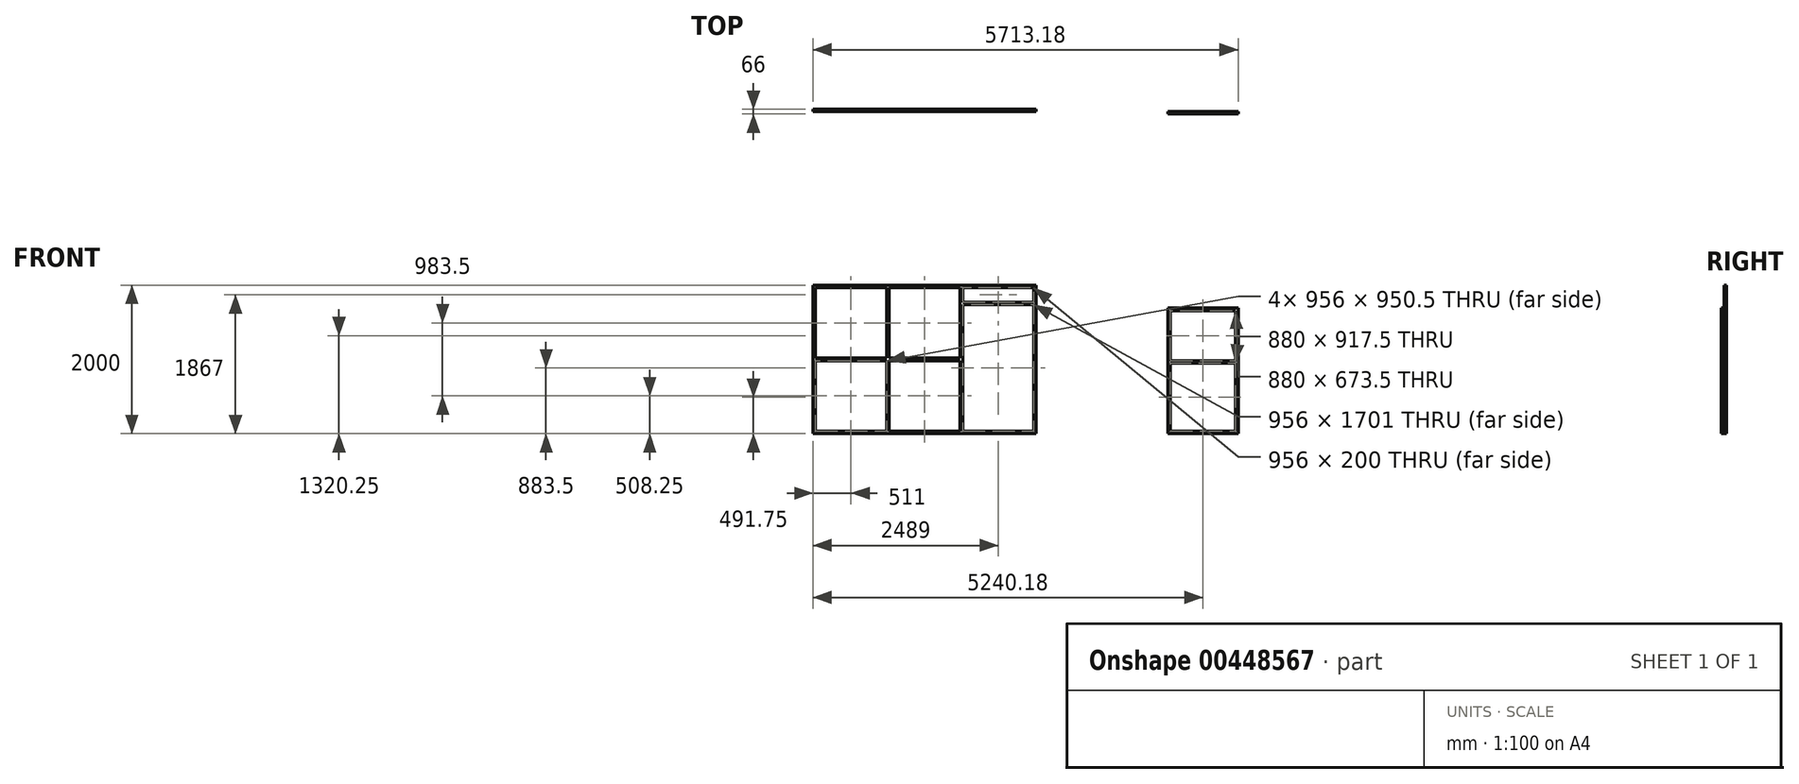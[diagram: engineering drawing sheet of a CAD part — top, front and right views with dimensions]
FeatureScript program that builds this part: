
annotation { "Feature Type Name" : "Feature", "Feature Type Description" : "" }
export const myFeature = defineFeature(function(context is Context, id is Id, definition is map)
    precondition{}
    {
        {
            var Q0;
            Q0=qCreatedBy(makeId("Front.planeOp"),FACE);
            var sketch = newSketch(context, id + "F0", { "sketchPlane" : qUnion([Q0])});
            skLineSegment(sketch, "E0.bottom", {"start": v(0, 0) * mm, "end": v(3000, 0) * mm});
            skLineSegment(sketch, "E0.top", {"start": v(0, 2000) * mm, "end": v(3000, 2000) * mm});
            skLineSegment(sketch, "E0.left", {"start": v(0, 0) * mm, "end": v(0, 2000) * mm});
            skLineSegment(sketch, "E0.right", {"start": v(3000, 0) * mm, "end": v(3000, 2000) * mm});
            skLineSegment(sketch, "E1.0", {"start": v(33, 33) * mm, "end": v(33, 1967) * mm});
            skLineSegment(sketch, "E1.1", {"start": v(33, 33) * mm, "end": v(2967, 33) * mm});
            skLineSegment(sketch, "E1.2", {"start": v(2967, 33) * mm, "end": v(2967, 1734) * mm});
            skLineSegment(sketch, "E1.3", {"start": v(33, 1967) * mm, "end": v(1978, 1967) * mm});
            skLineSegment(sketch, "E2.bottom", {"start": v(989, 1967) * mm, "end": v(1022, 1967) * mm});
            skLineSegment(sketch, "E2.top", {"start": v(989, 33) * mm, "end": v(1022, 33) * mm});
            skLineSegment(sketch, "E2.left", {"start": v(989, 1967) * mm, "end": v(989, 1016.5) * mm});
            skLineSegment(sketch, "E2.right", {"start": v(1022, 1967) * mm, "end": v(1022, 1016.5) * mm});
            skLineSegment(sketch, "E3.left", {"start": v(1978, 1967) * mm, "end": v(1978, 1016.5) * mm});
            skLineSegment(sketch, "E3.right", {"start": v(2011, 1967) * mm, "end": v(2011, 1767) * mm});
            skLineSegment(sketch, "E4.bottom", {"start": v(33, 1016.5) * mm, "end": v(989, 1016.5) * mm});
            skLineSegment(sketch, "E4.top", {"start": v(33, 983.5) * mm, "end": v(989, 983.5) * mm});
            skLineSegment(sketch, "E4.left", {"start": v(33, 1016.5) * mm, "end": v(33, 983.5) * mm});
            skLineSegment(sketch, "E4.right", {"start": v(2967, 1016.5) * mm, "end": v(2967, 983.5) * mm});
            skLineSegment(sketch, "E5.trimOffspring", {"start": v(1022, 983.5) * mm, "end": v(1978, 983.5) * mm});
            skLineSegment(sketch, "E6.trimOffspring", {"start": v(1022, 1016.5) * mm, "end": v(1978, 1016.5) * mm});
            skLineSegment(sketch, "E7.bottom", {"start": v(2011, 1767) * mm, "end": v(2967, 1767) * mm});
            skLineSegment(sketch, "E7.top", {"start": v(2011, 1734) * mm, "end": v(2967, 1734) * mm});
            skLineSegment(sketch, "E8.trimOffspring", {"start": v(1978, 983.5) * mm, "end": v(1978, 33) * mm});
            skLineSegment(sketch, "E9.trimOffspring", {"start": v(1022, 983.5) * mm, "end": v(1022, 33) * mm});
            skLineSegment(sketch, "E10.trimOffspring", {"start": v(989, 983.5) * mm, "end": v(989, 33) * mm});
            skLineSegment(sketch, "E11.trimOffspring", {"start": v(2011, 1734) * mm, "end": v(2011, 33) * mm});
            skLineSegment(sketch, "E12.trimOffspring", {"start": v(2967, 1767) * mm, "end": v(2967, 1967) * mm});
            skLineSegment(sketch, "E13.trimOffspring", {"start": v(2011, 1967) * mm, "end": v(2967, 1967) * mm});
            skSolve(sketch);
        }
        {
            var Q0;
            Q0 = qSketchRegion(id + "F0", true);
            var Q1;
            {var subQ5=sQuery(id+"F0.wireOp",EDGE,"E4.left");Q1=makeQuery(id+"F0.imprint","IMPRINT",FACE,{"disambiguationData":[TD([[makeQuery(id+"F0.imprint","IMPRINT",EDGE,{"derivedFrom":subQ5}),1.0]])]});}
            var Q2;
            {var subQ5=sQuery(id+"F0.wireOp",EDGE,"E2.bottom");Q2=makeQuery(id+"F0.imprint","IMPRINT",FACE,{"disambiguationData":[TD([[makeQuery(id+"F0.imprint","IMPRINT",EDGE,{"derivedFrom":subQ5}),-1.0]])]});}
            var Q3;
            Q3=makeQuery(id+"F0.imprint","IMPRINT",FACE,{"disambiguationData":[TD([[makeQuery(id+"F0.imprint","IMPRINT",EDGE,{"derivedFrom":sQuery(id+"F0.wireOp",EDGE,"E7.bottom")}),-1.0]])]});
            var Q4;
            {var subQ1=sQuery(id+"F0.wireOp",EDGE,"E3.bottom");Q4=makeQuery(id+"F0.imprint","IMPRINT",FACE,{"disambiguationData":[TD([[makeQuery(id+"F0.imprint","IMPRINT",EDGE,{"derivedFrom":subQ1}),-1.0]])]});}
            var Q5;
            {var subQ0=sQuery(id+"F0.wireOp",EDGE,"E3.top");Q5=makeQuery(id+"F0.imprint","IMPRINT",FACE,{"disambiguationData":[TD([[makeQuery(id+"F0.imprint","IMPRINT",EDGE,{"derivedFrom":subQ0}),1.0]])]});}
            var Q6;
            {var subQ0=sQuery(id+"F0.wireOp",EDGE,"E2.top");Q6=makeQuery(id+"F0.imprint","IMPRINT",FACE,{"disambiguationData":[TD([[makeQuery(id+"F0.imprint","IMPRINT",EDGE,{"derivedFrom":subQ0}),1.0]])]});}
            var Q7;
            {var subQ0=sQuery(id+"F0.wireOp",EDGE,"E4.bottom");var subQ1=sQuery(id+"F0.wireOp",EDGE,"E2.left");var subQ2=makeQuery(id+"F0.imprint","INTERSECT",VERTEX,{"derivedFrom":[subQ1,subQ0]});Q7=makeQuery(id+"F0.imprint","IMPRINT",FACE,{"disambiguationData":[TD([[makeQuery(id+"F0.imprint","IMPRINT",EDGE,{"disambiguationData":[TD([[subQ2,-1.0]])],"derivedFrom":subQ1}),1.0]])]});}
            var Q8;
            {var subQ0=sQuery(id+"F0.wireOp",EDGE,"E5.trimOffspring");var subQ1=sQuery(id+"F0.wireOp",EDGE,"E3.left");var subQ2=makeQuery(id+"F0.imprint","INTERSECT",VERTEX,{"derivedFrom":[subQ1,subQ0]});Q8=makeQuery(id+"F0.imprint","IMPRINT",FACE,{"disambiguationData":[TD([[makeQuery(id+"F0.imprint","IMPRINT",EDGE,{"disambiguationData":[TD([[subQ2,1.0]])],"derivedFrom":subQ1}),1.0]])]});}
            extrude(context, id + "F1", {"entities" : qUnion([Q0, Q1, Q2, Q3, Q4, Q5, Q6, Q7, Q8]), "depth" : 33 * mm});
        }
        {
            var Q0;
            Q0=makeQuery(id+"F1.opExtrude","CAP_FACE",FACE,{"disambiguationData":[OSD([sQuery(id+"F0.wireOp",EDGE,"E0.bottom"),sQuery(id+"F0.wireOp",EDGE,"E0.top"),sQuery(id+"F0.wireOp",EDGE,"E0.left"),sQuery(id+"F0.wireOp",EDGE,"E0.right"),sQuery(id+"F0.wireOp",EDGE,"E1.0"),sQuery(id+"F0.wireOp",EDGE,"E1.1"),sQuery(id+"F0.wireOp",EDGE,"E1.2"),sQuery(id+"F0.wireOp",EDGE,"E1.3"),sQuery(id+"F0.wireOp",EDGE,"E2.left"),sQuery(id+"F0.wireOp",EDGE,"E2.right"),sQuery(id+"F0.wireOp",EDGE,"E3.left"),sQuery(id+"F0.wireOp",EDGE,"E3.right"),sQuery(id+"F0.wireOp",EDGE,"E4.bottom"),sQuery(id+"F0.wireOp",EDGE,"E4.top"),sQuery(id+"F0.wireOp",EDGE,"E5.trimOffspring"),sQuery(id+"F0.wireOp",EDGE,"E6.trimOffspring"),sQuery(id+"F0.wireOp",EDGE,"E7.bottom"),sQuery(id+"F0.wireOp",EDGE,"E7.top")])],"isStart":false});
            var sketch = newSketch(context, id + "F2", { "sketchPlane" : qUnion([Q0])});
            skLineSegment(sketch, "E14.bottom", {"start": v(4767.18, 1690) * mm, "end": v(5713.18, 1690) * mm});
            skLineSegment(sketch, "E14.top", {"start": v(4767.18, 0) * mm, "end": v(5713.18, 0) * mm});
            skLineSegment(sketch, "E14.left", {"start": v(4767.18, 1690) * mm, "end": v(4767.18, 0) * mm});
            skLineSegment(sketch, "E14.right", {"start": v(5713.18, 1690) * mm, "end": v(5713.18, 0) * mm});
            skLineSegment(sketch, "E15.0", {"start": v(4800.18, 1657) * mm, "end": v(4800.18, 33) * mm});
            skLineSegment(sketch, "E15.1", {"start": v(4800.18, 1657) * mm, "end": v(5680.18, 1657) * mm});
            skLineSegment(sketch, "E15.2", {"start": v(5680.18, 1657) * mm, "end": v(5680.18, 33) * mm});
            skLineSegment(sketch, "E15.3", {"start": v(4800.18, 33) * mm, "end": v(5680.18, 33) * mm});
            skLineSegment(sketch, "E16.bottom", {"start": v(4800.18, 983.5) * mm, "end": v(5680.18, 983.5) * mm});
            skLineSegment(sketch, "E16.top", {"start": v(4800.18, 950.5) * mm, "end": v(5680.18, 950.5) * mm});
            skLineSegment(sketch, "E16.left", {"start": v(4800.18, 983.5) * mm, "end": v(4800.18, 950.5) * mm});
            skLineSegment(sketch, "E16.right", {"start": v(5680.18, 983.5) * mm, "end": v(5680.18, 950.5) * mm});
            skSolve(sketch);
        }
        {
            var Q0;
            Q0 = qSketchRegion(id + "F2", true);
            var Q1;
            Q1=makeQuery(id+"F2.imprint","IMPRINT",FACE,{"disambiguationData":[TD([[makeQuery(id+"F2.imprint","IMPRINT",EDGE,{"derivedFrom":sQuery(id+"F2.wireOp",EDGE,"E16.bottom")}),-1.0]])]});
            extrude(context, id + "F3", {"entities" : qUnion([Q0, Q1]), "depth" : 33 * mm});
        }
    });
